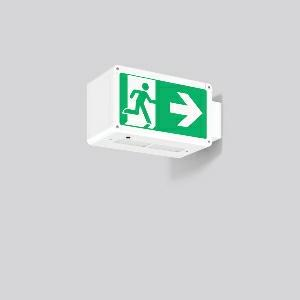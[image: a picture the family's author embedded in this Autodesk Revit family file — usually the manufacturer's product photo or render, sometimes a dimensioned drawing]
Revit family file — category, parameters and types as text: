
# Revit family: rechteck_wandausleger_671049_002_04_34b7
name_source: partatom
category: Lighting Fixtures
units: mm (PartAtom-declared; Revit-internal decimal feet)

## family parameters
Cut with Voids When Loaded = No
Host = Face
Light Source = No
Part Type = Normal
Room Calculation Point = No
Round Connector Dimension = Use Diameter
Shared = No

## types (1)
- RECHTECK wandausleger
    Apparent Load = 0 VA
    Default Elevation = 1800 mm
    Description = Series: RECHTECK
Rectangular wall extension luminaire in classic design. For escape route identification. Housing: aluminium, with plastic corner connectors. Display panels: plastic, opal, with motifs on one side/on both sides. Wall extension Electronic ballast included. Self-contained system with automatic self-test and feedback to the RZB monitoring system MULTIDIGIT. Please indicate legend number when placing your order! 
Colour: white
Length: 250 mm
Width: 125 mm
Height: 140 mm
Weight: 1.5 kg
Operating mode: maintained power mode
Viewing Distance: 21 m
Duration time: 3 h
Lamp: LED
Socket: without socket
Colour temperature: 6500K
Colour rendering index (CRI): 70
System power: 6.9 W
Control gear: Regulated power supply
Protection class: I
Type of protection: IP 44
    Height = 140 mm  [stored 0.459318 ft]
    Lamp = 0 x
    Length = 250 mm
    Luminous efficacy = 0 lm/W
    Manufacturer = RZB
    ModVariant = No
    Model = 671049.002.04
    Mounting Place = Wall
    Mounting Type = Surface mounted
    Number of Poles = 1
    OnlyDefault = Yes
    Power Factor = 1
    Product Name = RECHTECK wandausleger
    Product group = wall cantilever luminaires
    ProductGroupID = 2005
    Protection Class = Protection class I
    Protection Degree = IP 44
    RLX_Detail_Level = 1
    RLX_Emergency_Light_Flux = 0 lm
    RLX_Emergency_Type = 0
    RLX_Emergency_Type_DB = No
    RlxData = <blob elided: 22393 chars, md5=750edffe>
    Standby Power = 0 W
    System Light Flux = 0 lm
    System Power = 0 W
    Type Comments = Product without accessories
    Type Image = 671049.002.jpg
    URL = http://relux.com
    VarID = ---
    Voltage = 230 V
    Voltage Range = 220-240 V
    Weight = 0.00 kg
    Width = 125 mm

note: [stored X ft] marks values corroborated as IEEE doubles in the binary element streams (Revit-internal decimal feet)

## geometry (parser evidence)
native form markers: Blend x4, Sweep x11
no freeform markers — native parametric forms only
